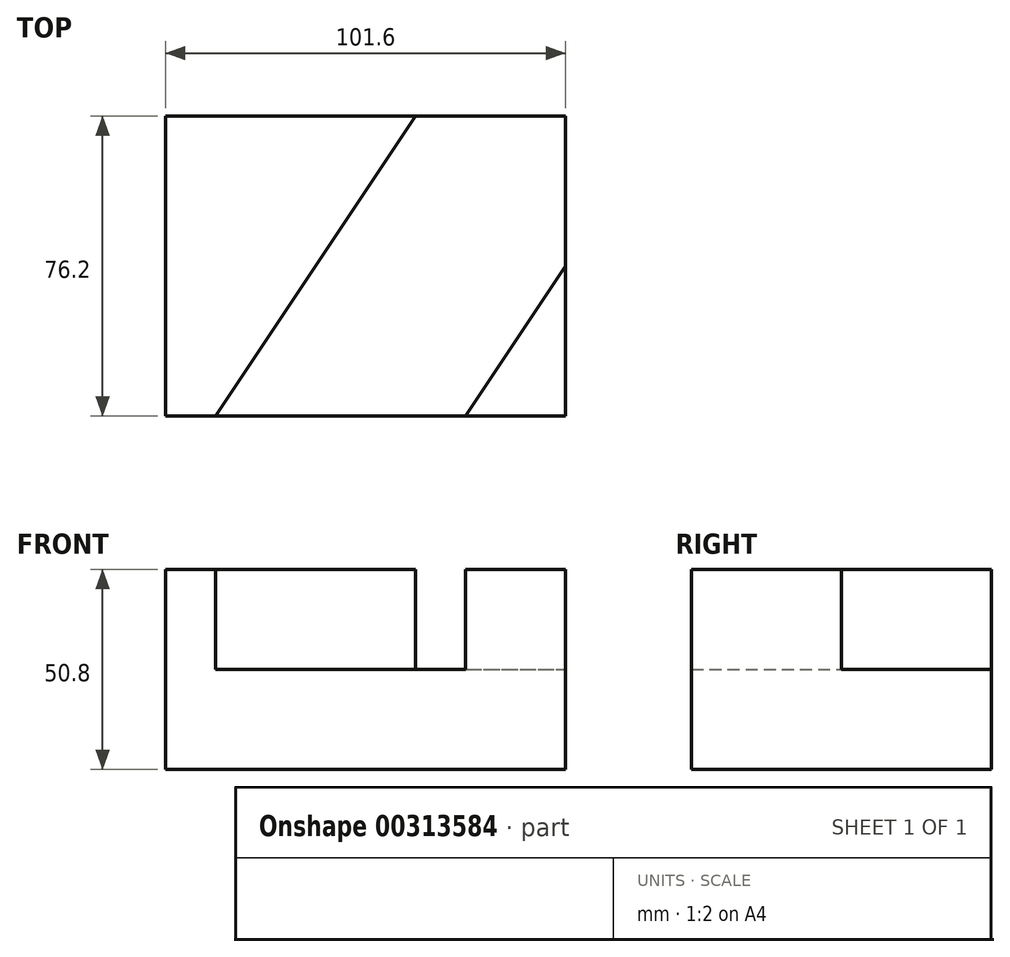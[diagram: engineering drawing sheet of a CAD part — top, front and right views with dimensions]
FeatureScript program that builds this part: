
annotation { "Feature Type Name" : "Feature", "Feature Type Description" : "" }
export const myFeature = defineFeature(function(context is Context, id is Id, definition is map)
    precondition{}
    {
        {
            var Q0;
            Q0=qCreatedBy(makeId("Top.planeOp"),FACE);
            var sketch = newSketch(context, id + "F0", { "sketchPlane" : qUnion([Q0])});
            skLineSegment(sketch, "E0", {"start": v(60.37, 35) * mm, "end": v(60.37, -41.2) * mm});
            skLineSegment(sketch, "E1", {"start": v(60.37, -41.2) * mm, "end": v(-41.23, -41.2) * mm});
            skLineSegment(sketch, "E2", {"start": v(-41.23, -41.2) * mm, "end": v(-41.23, 35) * mm});
            skLineSegment(sketch, "E3", {"start": v(-41.23, 35) * mm, "end": v(60.37, 35) * mm});
            skSolve(sketch);
        }
        {
            var Q0;
            Q0=makeQuery(id+"F0.imprint","IMPRINT",FACE,{"disambiguationData":[TD([[makeQuery(id+"F0.imprint","IMPRINT",EDGE,{"derivedFrom":sQuery(id+"F0.wireOp",EDGE,"E0")}),-1.0]])]});
            extrude(context, id + "F1", {"entities" : qUnion([Q0]), "oppositeDirection" : true, "depth" : 25.4 * mm});
        }
        {
            var Q0;
            Q0=makeQuery(id+"F1.opExtrude","CAP_FACE",FACE,{"disambiguationData":[OSD([sQuery(id+"F0.wireOp",EDGE,"E0"),sQuery(id+"F0.wireOp",EDGE,"E1"),sQuery(id+"F0.wireOp",EDGE,"E2"),sQuery(id+"F0.wireOp",EDGE,"E3")])],"isStart":true});
            var sketch = newSketch(context, id + "F2", { "sketchPlane" : qUnion([Q0])});
            skLineSegment(sketch, "E4", {"start": v(60.37, -41.2) * mm, "end": v(34.97, -41.2) * mm});
            skLineSegment(sketch, "E5", {"start": v(34.97, -41.2) * mm, "end": v(60.37, -3.1) * mm});
            skLineSegment(sketch, "E6", {"start": v(60.37, -3.1) * mm, "end": v(60.37, -41.2) * mm});
            skLineSegment(sketch, "E7", {"start": v(-41.23, -41.2) * mm, "end": v(-28.53, -41.2) * mm});
            skLineSegment(sketch, "E8", {"start": v(-28.53, -41.2) * mm, "end": v(22.27, 35) * mm});
            skLineSegment(sketch, "E9", {"start": v(22.27, 35) * mm, "end": v(-41.23, 35) * mm});
            skLineSegment(sketch, "E10", {"start": v(-41.23, 35) * mm, "end": v(-41.23, -41.2) * mm});
            skSolve(sketch);
        }
        {
            var Q0;
            Q0=makeQuery(id+"F2.imprint","IMPRINT",FACE,{"disambiguationData":[TD([[makeQuery(id+"F2.imprint","IMPRINT",EDGE,{"derivedFrom":sQuery(id+"F2.wireOp",EDGE,"E7")}),-1.0]])]});
            var Q1;
            Q1=makeQuery(id+"F2.imprint","IMPRINT",FACE,{"disambiguationData":[TD([[makeQuery(id+"F2.imprint","IMPRINT",EDGE,{"derivedFrom":sQuery(id+"F2.wireOp",EDGE,"E4")}),-1.0]])]});
            extrude(context, id + "F3", {"entities" : qUnion([Q0, Q1]), "operationType" : NewBodyOperationType.ADD, "depth" : 25.4 * mm});
        }
    });
